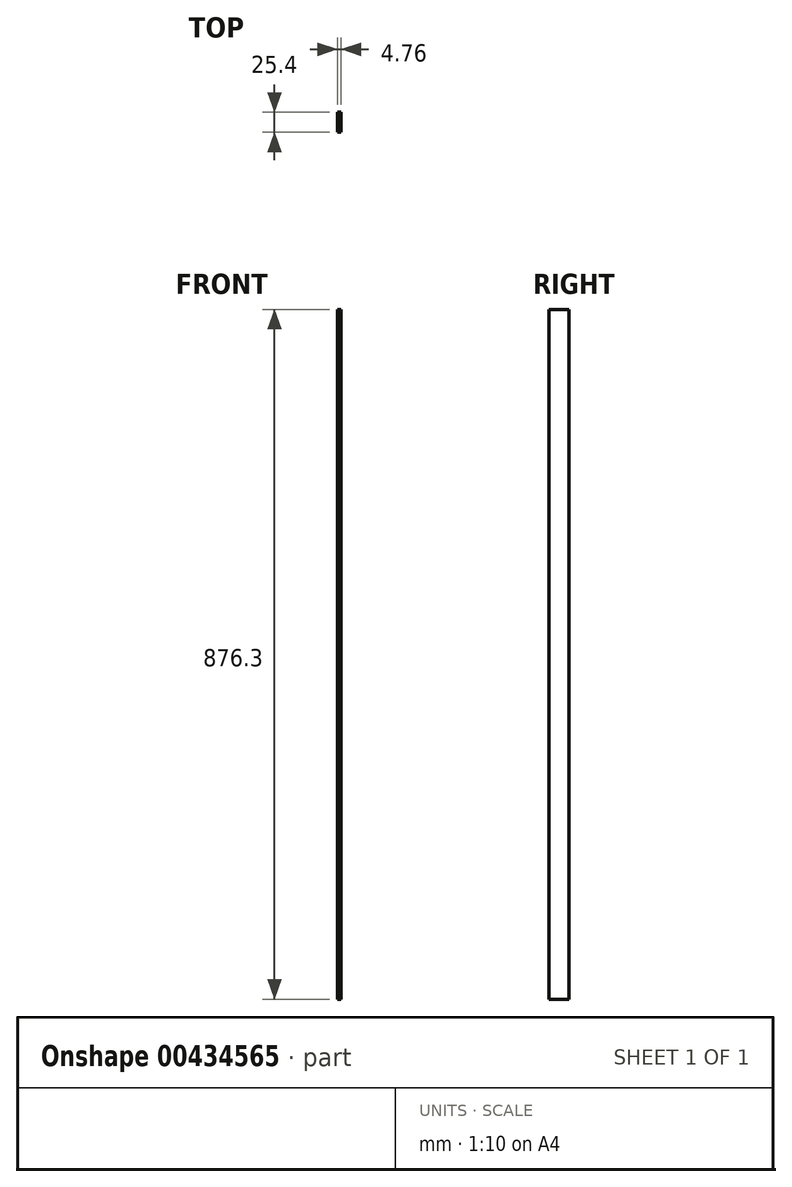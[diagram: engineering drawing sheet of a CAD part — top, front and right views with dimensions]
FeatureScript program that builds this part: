
annotation { "Feature Type Name" : "Feature", "Feature Type Description" : "" }
export const myFeature = defineFeature(function(context is Context, id is Id, definition is map)
    precondition{}
    {
        {
            var Q0;
            Q0=qCreatedBy(makeId("Right.planeOp"),FACE);
            var sketch = newSketch(context, id + "F0", { "sketchPlane" : qUnion([Q0])});
            skLineSegment(sketch, "E0.bottom", {"start": v(-63.17, 911.63) * mm, "end": v(-37.77, 911.63) * mm});
            skLineSegment(sketch, "E0.top", {"start": v(-63.17, 35.33) * mm, "end": v(-37.77, 35.33) * mm});
            skLineSegment(sketch, "E0.left", {"start": v(-63.17, 911.63) * mm, "end": v(-63.17, 35.33) * mm});
            skLineSegment(sketch, "E0.right", {"start": v(-37.77, 911.63) * mm, "end": v(-37.77, 35.33) * mm});
            skSolve(sketch);
        }
        {
            var Q0;
            Q0=makeQuery(id+"F0.imprint","IMPRINT",FACE,{"disambiguationData":[TD([[makeQuery(id+"F0.imprint","IMPRINT",EDGE,{"derivedFrom":sQuery(id+"F0.wireOp",EDGE,"E0.bottom")}),-1.0]])]});
            extrude(context, id + "F1", {"entities" : qUnion([Q0]), "depth" : 4.76 * mm});
        }
    });
